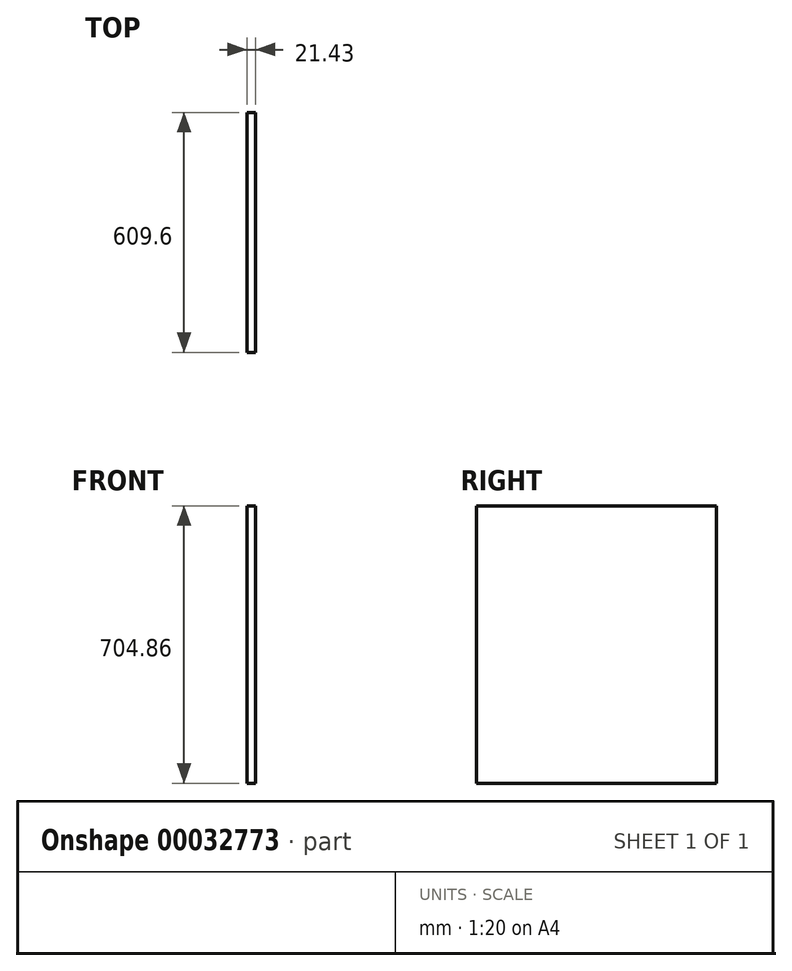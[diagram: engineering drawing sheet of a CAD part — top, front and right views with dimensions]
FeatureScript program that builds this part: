
annotation { "Feature Type Name" : "Feature", "Feature Type Description" : "" }
export const myFeature = defineFeature(function(context is Context, id is Id, definition is map)
    precondition{}
    {
        {
            var Q0;
            Q0=qCreatedBy(makeId("Right.planeOp"),FACE);
            var sketch = newSketch(context, id + "F0", { "sketchPlane" : qUnion([Q0])});
            skLineSegment(sketch, "E0.bottom", {"start": v(-304.8, 352.43) * mm, "end": v(304.8, 352.43) * mm});
            skLineSegment(sketch, "E0.top", {"start": v(-304.8, -352.43) * mm, "end": v(304.8, -352.43) * mm});
            skLineSegment(sketch, "E0.left", {"start": v(-304.8, 352.43) * mm, "end": v(-304.8, -352.43) * mm});
            skLineSegment(sketch, "E0.right", {"start": v(304.8, 352.43) * mm, "end": v(304.8, -352.43) * mm});
            skLineSegment(sketch, "E1", {"start": v(0, -352.43) * mm, "end": v(0, 352.43) * mm, "construction": true});
            skSolve(sketch);
        }
        {
            var Q0;
            Q0 = qSketchRegion(id + "F0", true);
            extrude(context, id + "F1", {"entities" : qUnion([Q0]), "depth" : 21.43 * mm});
        }
    });
